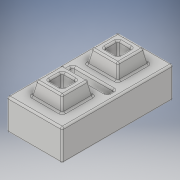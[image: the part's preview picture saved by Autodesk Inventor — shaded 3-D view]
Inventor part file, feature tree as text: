
AUTODESK INVENTOR PART (.ipt)
format: ipt  version: 2019 (Build 230136000, 136)  size: 357,376 bytes
history: native  units: in
note: dims shown in document units (in); Inventor stores cm internally (conversion verified against a paired STEP export)
features: extrude x5, sketch x5, fillet x3
ambient origin geometry x8: Origin, YZ Plane, XZ Plane, XY Plane, X Axis, Y Axis, Z Axis, Center Point
bodies: Solid1 (feature_tree)
feature tree (13):
  extrude  "Extrusion1"  Depth=8.0in
  extrude  "Extrusion2"  Depth=2.25in
  sketch  "Sketch3"  dims[d4=2.25in d5=2.25in d6=0.0in]
  extrude  "Extrusion4"  Depth=2.25in
  fillet  "Fillet1"  [1 undecoded]
  extrude  "Extrusion5"  Depth=2.0in
  extrude  "Extrusion11"  Depth=0.125in TaperAngle=0.0deg
  fillet  "Fillet2"  Radius=1.0in
  fillet  "Fillet3"  Radius=0.125in
  sketch  "Sketch1"  dims[d0=4.0in d1=8.0in]
  sketch  "Sketch2"  dims[d2=2.25in d3=2.25in]
  sketch  "Sketch7"  dims[d7=2.0in d8=2.0in]
  sketch  "Sketch13"  dims[d9=1.5in d10=0.0in d11=0.75in d12=0.0in d39=1.0in d40=-0.073in d41=0.125in d42=1.0in d43=1.0in d44=0.0in d45=2.0in d46=1.0in d47=1.0in d48=0.0in d49=2.0in d50=3.0in d51=0.0in d93=3.0in d94=0.5in d95=2.25in d96=0.0in d97=0.125in d98=0.125in]
note: 1 required parameter value undecoded (feature->parameter linkage not recoverable at this tier; creation-order binding heuristic only, values carry confidence <= 0.55)
